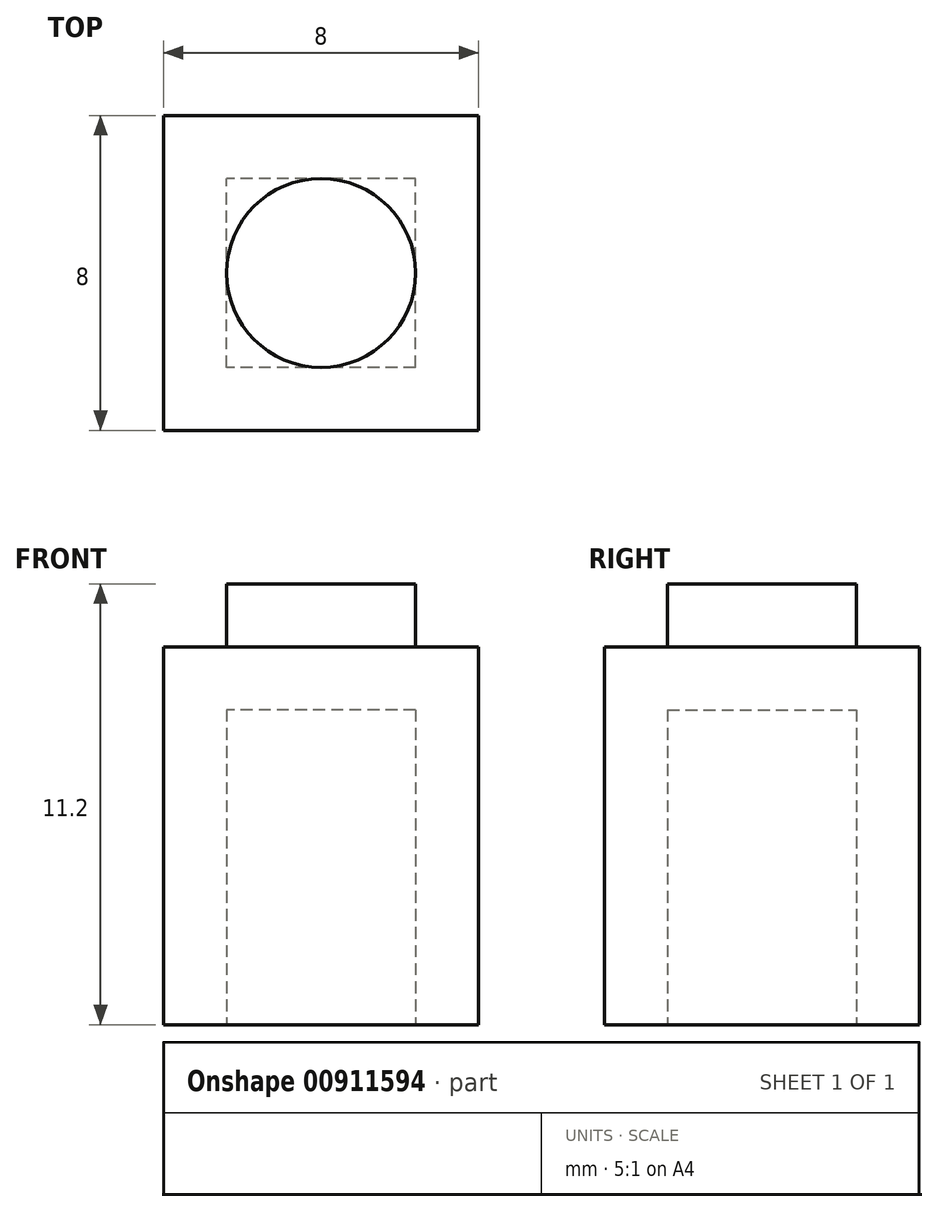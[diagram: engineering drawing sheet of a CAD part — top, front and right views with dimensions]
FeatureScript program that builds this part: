
annotation { "Feature Type Name" : "Feature", "Feature Type Description" : "" }
export const myFeature = defineFeature(function(context is Context, id is Id, definition is map)
    precondition{}
    {
        {
            var Q0;
            Q0=qCreatedBy(makeId("Top.planeOp"),FACE);
            var sketch = newSketch(context, id + "F0", { "sketchPlane" : qUnion([Q0])});
            skLineSegment(sketch, "E0.bottom", {"start": v(4, 4) * mm, "end": v(-4, 4) * mm});
            skLineSegment(sketch, "E0.top", {"start": v(4, -4) * mm, "end": v(-4, -4) * mm});
            skLineSegment(sketch, "E0.left", {"start": v(4, 4) * mm, "end": v(4, -4) * mm});
            skLineSegment(sketch, "E0.right", {"start": v(-4, 4) * mm, "end": v(-4, -4) * mm});
            skPoint(sketch, "E0.middle", {"position": v(0, 0) * mm});
            skSolve(sketch);
        }
        {
            var Q0;
            Q0=makeQuery(id+"F0.imprint","IMPRINT",FACE,{"disambiguationData":[TD([[makeQuery(id+"F0.imprint","IMPRINT",EDGE,{"derivedFrom":sQuery(id+"F0.wireOp",EDGE,"E0.bottom")}),1.0]])]});
            extrude(context, id + "F1", {"entities" : qUnion([Q0]), "depth" : 9.6 * mm, "offsetDistance" : 25 * mm});
        }
        {
            var Q0;
            Q0=makeQuery(id+"F1.opExtrude","CAP_FACE",FACE,{"disambiguationData":[OSD([sQuery(id+"F0.wireOp",EDGE,"E0.bottom"),sQuery(id+"F0.wireOp",EDGE,"E0.top"),sQuery(id+"F0.wireOp",EDGE,"E0.left"),sQuery(id+"F0.wireOp",EDGE,"E0.right")])],"isStart":true});
            var sketch = newSketch(context, id + "F2", { "sketchPlane" : qUnion([Q0])});
            skLineSegment(sketch, "E1.bottom", {"start": v(2.4, 2.4) * mm, "end": v(-2.4, 2.4) * mm});
            skLineSegment(sketch, "E1.top", {"start": v(2.4, -2.4) * mm, "end": v(-2.4, -2.4) * mm});
            skLineSegment(sketch, "E1.left", {"start": v(2.4, 2.4) * mm, "end": v(2.4, -2.4) * mm});
            skLineSegment(sketch, "E1.right", {"start": v(-2.4, 2.4) * mm, "end": v(-2.4, -2.4) * mm});
            skPoint(sketch, "E1.middle", {"position": v(0, 0) * mm});
            skSolve(sketch);
        }
        {
            var Q0;
            Q0=makeQuery(id+"F2.imprint","IMPRINT",FACE,{"disambiguationData":[TD([[makeQuery(id+"F2.imprint","IMPRINT",EDGE,{"derivedFrom":sQuery(id+"F2.wireOp",EDGE,"E1.bottom")}),1.0]])]});
            extrude(context, id + "F3", {"entities" : qUnion([Q0]), "operationType" : NewBodyOperationType.REMOVE, "oppositeDirection" : true, "depth" : 8 * mm, "offsetDistance" : 25 * mm});
        }
        {
            var Q0;
            Q0=makeQuery(id+"F1.opExtrude","CAP_FACE",FACE,{"disambiguationData":[OSD([sQuery(id+"F0.wireOp",EDGE,"E0.bottom"),sQuery(id+"F0.wireOp",EDGE,"E0.top"),sQuery(id+"F0.wireOp",EDGE,"E0.left"),sQuery(id+"F0.wireOp",EDGE,"E0.right")])],"isStart":false});
            var sketch = newSketch(context, id + "F4", { "sketchPlane" : qUnion([Q0])});
            skCircle(sketch, "E2", {"center": v(0, 0) * mm, "radius": 2.4 * mm});
            skSolve(sketch);
        }
        {
            var Q0;
            Q0=makeQuery(id+"F4.imprint","IMPRINT",FACE,{"disambiguationData":[TD([[makeQuery(id+"F4.imprint","IMPRINT",EDGE,{"derivedFrom":sQuery(id+"F4.wireOp",EDGE,"E2")}),1.0]])]});
            extrude(context, id + "F5", {"entities" : qUnion([Q0]), "operationType" : NewBodyOperationType.ADD, "depth" : 1.6 * mm, "offsetDistance" : 25 * mm});
        }
    });
